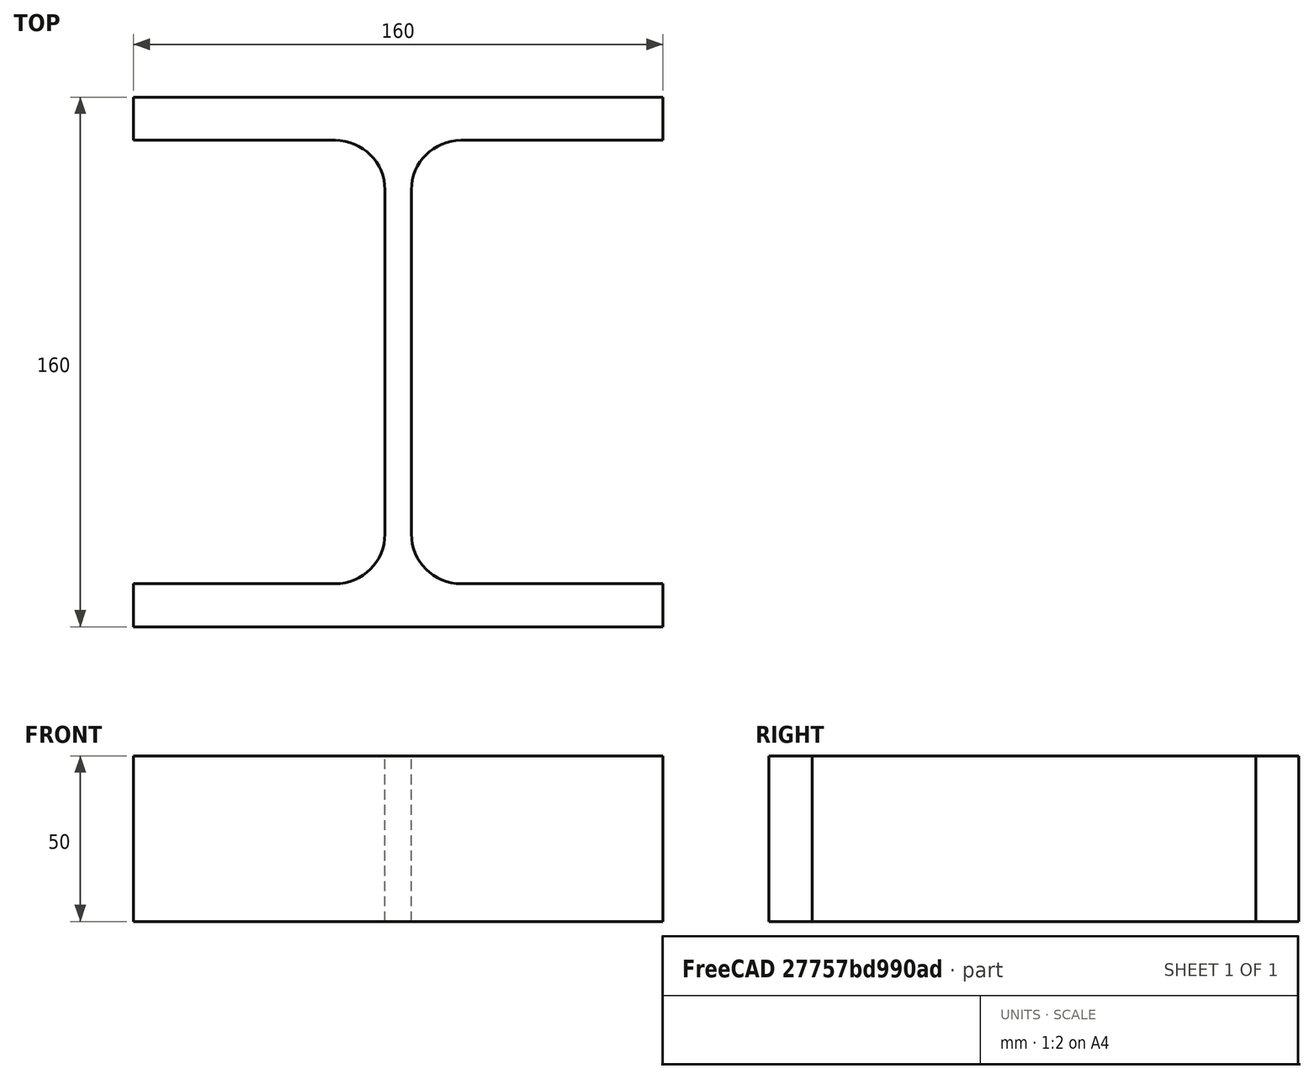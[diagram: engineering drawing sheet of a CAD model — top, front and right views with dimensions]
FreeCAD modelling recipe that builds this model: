
FCSTD DOCUMENT  (FreeCAD 0.15R4671 (Git))
Label: HE-B-Profile 160 DIN1025-2 S235JR
License: All rights reserved
LicenseURL: http://en.wikipedia.org/wiki/All_rights_reserved
objects: Sketcher::SketchObject×1, Part::Extrusion×1
note: 2 computed .brp shape members not serialized (recipe doc carries the construction recipe); baked Part::Feature solids carry a one-line shape summary decoded from their .brp

FEATURE [Sketcher::SketchObject] Sketch
  sketch-geometry (16):
    g0: LineSegment StartX=4 StartY=-52 StartZ=0 EndX=4 EndY=52 EndZ=0
    g1: LineSegment StartX=19 StartY=67 StartZ=0 EndX=80 EndY=67 EndZ=0
    g2: LineSegment StartX=80 StartY=67 StartZ=0 EndX=80 EndY=80 EndZ=0
    g3: LineSegment StartX=80 StartY=80 StartZ=0 EndX=-80 EndY=80 EndZ=0
    g4: LineSegment StartX=-80 StartY=80 StartZ=0 EndX=-80 EndY=67 EndZ=0
    g5: LineSegment StartX=-80 StartY=67 StartZ=0 EndX=-19 EndY=67 EndZ=0
    g6: LineSegment StartX=-4 StartY=52 StartZ=0 EndX=-4 EndY=-52 EndZ=0
    g7: LineSegment StartX=-19 StartY=-67 StartZ=0 EndX=-80 EndY=-67 EndZ=0
    g8: LineSegment StartX=-80 StartY=-67 StartZ=0 EndX=-80 EndY=-80 EndZ=0
    g9: LineSegment StartX=-80 StartY=-80 StartZ=0 EndX=80 EndY=-80 EndZ=0
    g10: LineSegment StartX=80 StartY=-80 StartZ=0 EndX=80 EndY=-67 EndZ=0
    g11: LineSegment StartX=80 StartY=-67 StartZ=0 EndX=19 EndY=-67 EndZ=0
    g12: ArcOfCircle CenterX=19 CenterY=52 CenterZ=0 NormalX=0 NormalY=0 NormalZ=1 Radius=15 StartAngle=1.5708 EndAngle=3.14159
    g13: ArcOfCircle CenterX=19 CenterY=-52 CenterZ=0 NormalX=0 NormalY=0 NormalZ=1 Radius=15 StartAngle=3.14159 EndAngle=4.71239
    g14: ArcOfCircle CenterX=-19 CenterY=52 CenterZ=0 NormalX=0 NormalY=0 NormalZ=1 Radius=15 StartAngle=0 EndAngle=1.5708
    g15: ArcOfCircle CenterX=-19 CenterY=-52 CenterZ=0 NormalX=0 NormalY=0 NormalZ=1 Radius=15 StartAngle=4.71239 EndAngle=6.28319
  constraints (42):
    c: Vertical(g0)
    c: Coincident(g2,g1)
    c: Vertical(g2)
    c: Coincident(g3,g2)
    c: Coincident(g4,g3)
    c: Vertical(g4)
    c: Coincident(g5,g4)
    c: Horizontal(g5)
    c: Vertical(g6)
    c: Horizontal(g7)
    c: Coincident(g8,g7)
    c: Vertical(g8)
    c: Coincident(g9,g8)
    c: Horizontal(g9)
    c: Coincident(g10,g9)
    c: Vertical(g10)
    c: Coincident(g11,g10)
    c: Horizontal(g11)
    c: Tangent(g1,g12) = 1.5708
    c: Tangent(g0,g12) = 1.5708
    c: Tangent(g0,g13) = 1.5708
    c: Tangent(g11,g13) = 1.5708
    c: Tangent(g5,g14) = 1.5708
    c: Tangent(g6,g14) = 1.5708
    c: Tangent(g6,g15) = 1.5708
    c: Tangent(g7,g15) = 1.5708
    c: Equal(g3,g9)
    c: Equal(g2,g4)
    c: Equal(g4,g8)
    c: Equal(g8,g10)
    c: Equal(g12,g14)
    c: Equal(g14,g15)
    c: Equal(g15,g13)
    c: Symmetric(g2,g3,g-2)
    c: Symmetric(g9,g8,g-2)
    c: Symmetric(g0,g6,g-2)
    c: Symmetric(g2,g9,g-1)
    c: DistanceY(g2,g9) = -160
    c: DistanceX(g3) = -160
    c: DistanceX(g0,g6) = -8
    c: DistanceY(g2) = 13
    c: Radius(g12) = 15
FEATURE [Part::Extrusion] Extrude  label="HE-B-Profile 160 DIN1025-2 S235JR"
  Base = -> Sketch
  Dir = (0,0,50)
  Solid = true
